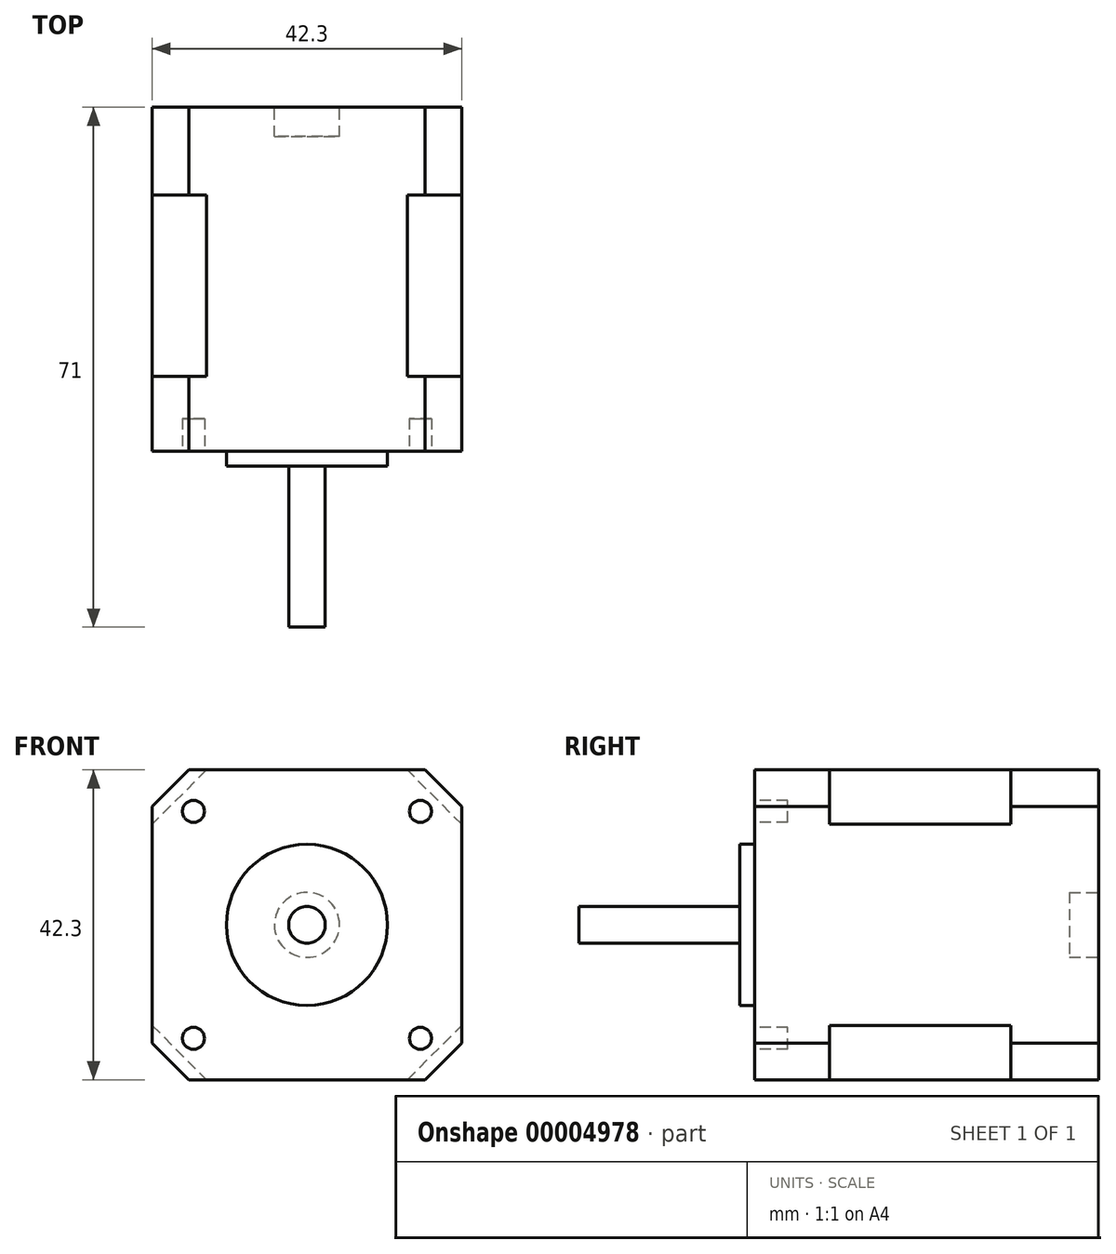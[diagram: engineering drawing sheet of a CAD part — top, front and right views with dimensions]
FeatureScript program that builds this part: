
annotation { "Feature Type Name" : "Feature", "Feature Type Description" : "" }
export const myFeature = defineFeature(function(context is Context, id is Id, definition is map)
    precondition{}
    {
        {
            var Q0;
            Q0=qCreatedBy(makeId("Front.planeOp"),FACE);
            var sketch = newSketch(context, id + "F0", { "sketchPlane" : qUnion([Q0])});
            skLineSegment(sketch, "E0.rect.bottom", {"start": v(21.15, 21.15) * mm, "end": v(-21.15, 21.15) * mm});
            skLineSegment(sketch, "E0.rect.top", {"start": v(21.15, -21.15) * mm, "end": v(-21.15, -21.15) * mm});
            skLineSegment(sketch, "E0.rect.left", {"start": v(21.15, 21.15) * mm, "end": v(21.15, -21.15) * mm});
            skLineSegment(sketch, "E0.rect.right", {"start": v(-21.15, 21.15) * mm, "end": v(-21.15, -21.15) * mm});
            skPoint(sketch, "E0.rect.middle", {"position": v(0, 0) * mm});
            skSolve(sketch);
        }
        {
            var Q0;
            Q0 = qSketchRegion(id + "F0", true);
            extrude(context, id + "F1", {"entities" : qUnion([Q0]), "depth" : 47 * mm});
        }
        {
            var Q0;
            Q0=makeQuery(id+"F1.opExtrude","CAP_FACE",FACE,{"disambiguationData":[OSD([sQuery(id+"F0.wireOp",EDGE,"E0.rect.bottom"),sQuery(id+"F0.wireOp",EDGE,"E0.rect.top"),sQuery(id+"F0.wireOp",EDGE,"E0.rect.left"),sQuery(id+"F0.wireOp",EDGE,"E0.rect.right")])],"isStart":false});
            var sketch = newSketch(context, id + "F2", { "sketchPlane" : qUnion([Q0])});
            skLineSegment(sketch, "E1", {"start": v(0, 21.15) * mm, "end": v(0, -21.15) * mm, "construction": true});
            skLineSegment(sketch, "E2", {"start": v(-21.15, 0) * mm, "end": v(21.15, 0) * mm, "construction": true});
            skLineSegment(sketch, "E3", {"start": v(-21.15, 21.15) * mm, "end": v(0, 0) * mm, "construction": true});
            skCircle(sketch, "E4", {"center": v(-15.5, 15.5) * mm, "radius": 1.5 * mm});
            skCircle(sketch, "E5.1.0", {"center": v(-15.5, -15.5) * mm, "radius": 1.5 * mm});
            skCircle(sketch, "E5.2.0", {"center": v(15.5, -15.5) * mm, "radius": 1.5 * mm});
            skPoint(sketch, "E5.center", {"position": v(0, 0) * mm});
            skCircle(sketch, "E6.1.3.0", {"center": v(15.5, 15.5) * mm, "radius": 1.5 * mm});
            skSolve(sketch);
        }
        {
            var Q0;
            Q0 = qSketchRegion(id + "F2", true);
            extrude(context, id + "F3", {"entities" : qUnion([Q0]), "operationType" : NewBodyOperationType.REMOVE, "oppositeDirection" : true, "depth" : 4.5 * mm});
        }
        {
            var Q0;
            Q0=makeQuery(id+"F1.opExtrude","CAP_FACE",FACE,{"disambiguationData":[OSD([sQuery(id+"F0.wireOp",EDGE,"E0.rect.bottom"),sQuery(id+"F0.wireOp",EDGE,"E0.rect.top"),sQuery(id+"F0.wireOp",EDGE,"E0.rect.left"),sQuery(id+"F0.wireOp",EDGE,"E0.rect.right")])],"isStart":false});
            var sketch = newSketch(context, id + "F4", { "sketchPlane" : qUnion([Q0])});
            skLineSegment(sketch, "E7", {"start": v(0, 21.15) * mm, "end": v(0, -21.15) * mm, "construction": true});
            skCircle(sketch, "E8", {"center": v(0, 0) * mm, "radius": 11 * mm});
            skSolve(sketch);
        }
        {
            var Q0;
            Q0 = qSketchRegion(id + "F4", true);
            extrude(context, id + "F5", {"entities" : qUnion([Q0]), "depth" : 2 * mm});
        }
        {
            var Q0;
            Q0=makeQuery(id+"F5.opExtrude","CAP_FACE",FACE,{"disambiguationData":[OSD([sQuery(id+"F4.wireOp",EDGE,"E8")])],"isStart":false});
            var sketch = newSketch(context, id + "F6", { "sketchPlane" : qUnion([Q0])});
            skCircle(sketch, "E9", {"center": v(0, 0) * mm, "radius": 2.5 * mm});
            skSolve(sketch);
        }
        {
            var Q0;
            Q0 = qSketchRegion(id + "F6", true);
            extrude(context, id + "F7", {"entities" : qUnion([Q0]), "operationType" : NewBodyOperationType.ADD, "depth" : 22 * mm});
        }
        {
            var Q0;
            Q0=makeQuery(id+"F1.opExtrude","SWEPT_EDGE",EDGE,{"disambiguationData":[OSD([sQuery(id+"F0.wireOp",EDGE,"E0.rect.bottom"),sQuery(id+"F0.wireOp",EDGE,"E0.rect.left")])]});
            var Q1;
            Q1=makeQuery(id+"F1.opExtrude","SWEPT_EDGE",EDGE,{"disambiguationData":[OSD([sQuery(id+"F0.wireOp",EDGE,"E0.rect.bottom"),sQuery(id+"F0.wireOp",EDGE,"E0.rect.right")])]});
            var Q2;
            Q2=makeQuery(id+"F1.opExtrude","SWEPT_EDGE",EDGE,{"disambiguationData":[OSD([sQuery(id+"F0.wireOp",EDGE,"E0.rect.top"),sQuery(id+"F0.wireOp",EDGE,"E0.rect.left")])]});
            var Q3;
            Q3=makeQuery(id+"F1.opExtrude","SWEPT_EDGE",EDGE,{"disambiguationData":[OSD([sQuery(id+"F0.wireOp",EDGE,"E0.rect.top"),sQuery(id+"F0.wireOp",EDGE,"E0.rect.right")])]});
            chamfer(context, id + "F8", {"entities" : qUnion([Q0, Q1, Q2, Q3]), "width" : 5 * mm, "tangentPropagation" : true});
        }
        {
            var Q0;
            Q0=makeQuery(id+"F1.opExtrude","CAP_FACE",FACE,{"disambiguationData":[OSD([sQuery(id+"F0.wireOp",EDGE,"E0.rect.bottom"),sQuery(id+"F0.wireOp",EDGE,"E0.rect.top"),sQuery(id+"F0.wireOp",EDGE,"E0.rect.left"),sQuery(id+"F0.wireOp",EDGE,"E0.rect.right")])],"isStart":true});
            cPlane(context, id + "F9", {"entities" : qUnion([Q0]), "cplaneType" : CPlaneType.OFFSET, "offset" : 12 * mm, "oppositeDirection" : true, "width" : 150 * mm, "height" : 150 * mm});
        }
        {
            var Q0;
            Q0=qCreatedBy(id+"F9.planeOp",FACE);
            var sketch = newSketch(context, id + "F10", { "sketchPlane" : qUnion([Q0])});
            skLineSegment(sketch, "E10.0", {"start": v(-16.15, 21.15) * mm, "end": v(16.15, 21.15) * mm, "construction": true});
            skLineSegment(sketch, "E10.1", {"start": v(-16.15, 21.15) * mm, "end": v(-21.15, 16.15) * mm});
            skLineSegment(sketch, "E10.2", {"start": v(-21.15, 16.15) * mm, "end": v(-21.15, -16.15) * mm, "construction": true});
            skLineSegment(sketch, "E11", {"start": v(-21.15, 13.73) * mm, "end": v(-13.73, 21.15) * mm});
            skLineSegment(sketch, "E12", {"start": v(-13.73, 21.15) * mm, "end": v(-16.15, 21.15) * mm});
            skLineSegment(sketch, "E13", {"start": v(-21.15, 16.15) * mm, "end": v(-21.15, 13.73) * mm});
            skLineSegment(sketch, "E14.1.0", {"start": v(-16.15, -21.15) * mm, "end": v(-13.73, -21.15) * mm});
            skLineSegment(sketch, "E14.1.1", {"start": v(-13.73, -21.15) * mm, "end": v(-21.15, -13.73) * mm});
            skLineSegment(sketch, "E14.1.2", {"start": v(-21.15, -13.73) * mm, "end": v(-21.15, -16.15) * mm});
            skLineSegment(sketch, "E14.1.3", {"start": v(-21.15, -16.15) * mm, "end": v(-16.15, -21.15) * mm});
            skLineSegment(sketch, "E14.2.0", {"start": v(21.15, -16.15) * mm, "end": v(21.15, -13.73) * mm});
            skLineSegment(sketch, "E14.2.1", {"start": v(21.15, -13.73) * mm, "end": v(13.73, -21.15) * mm});
            skLineSegment(sketch, "E14.2.2", {"start": v(13.73, -21.15) * mm, "end": v(16.15, -21.15) * mm});
            skLineSegment(sketch, "E14.2.3", {"start": v(16.15, -21.15) * mm, "end": v(21.15, -16.15) * mm});
            skPoint(sketch, "E14.center", {"position": v(0, 0) * mm});
            skLineSegment(sketch, "E15.2.3.0", {"start": v(16.15, 21.15) * mm, "end": v(13.73, 21.15) * mm});
            skLineSegment(sketch, "E15.3.3.0", {"start": v(13.73, 21.15) * mm, "end": v(21.15, 13.73) * mm});
            skLineSegment(sketch, "E15.6.3.0", {"start": v(21.15, 13.73) * mm, "end": v(21.15, 16.15) * mm});
            skLineSegment(sketch, "E15.9.3.0", {"start": v(21.15, 16.15) * mm, "end": v(16.15, 21.15) * mm});
            skSolve(sketch);
        }
        {
            var Q0;
            Q0 = qSketchRegion(id + "F10", true);
            extrude(context, id + "F11", {"entities" : qUnion([Q0]), "operationType" : NewBodyOperationType.REMOVE, "oppositeDirection" : true, "depth" : 24.75 * mm});
        }
        {
            var Q0;
            Q0=makeQuery(id+"F1.opExtrude","CAP_FACE",FACE,{"disambiguationData":[OSD([sQuery(id+"F0.wireOp",EDGE,"E0.rect.bottom"),sQuery(id+"F0.wireOp",EDGE,"E0.rect.top"),sQuery(id+"F0.wireOp",EDGE,"E0.rect.left"),sQuery(id+"F0.wireOp",EDGE,"E0.rect.right")])],"isStart":true});
            var sketch = newSketch(context, id + "F12", { "sketchPlane" : qUnion([Q0])});
            skCircle(sketch, "E16", {"center": v(0, 0) * mm, "radius": 4.44 * mm});
            skSolve(sketch);
        }
        {
            var Q0;
            Q0 = qSketchRegion(id + "F12", true);
            extrude(context, id + "F13", {"entities" : qUnion([Q0]), "operationType" : NewBodyOperationType.REMOVE, "oppositeDirection" : true, "depth" : 4 * mm});
        }
    });
